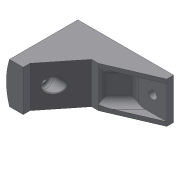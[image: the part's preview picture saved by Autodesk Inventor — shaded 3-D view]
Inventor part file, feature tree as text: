
AUTODESK INVENTOR PART (.ipt)
format: ipt  version: 2018 (Build 220112000, 112)  size: 190,464 bytes
history: native  units: mm
features: sketch x7, extrude x5, projected_geometry x5, fillet x3, hole x2, chamfer x2, mirror x1
ambient origin geometry x8: Origin, YZ Plane, XZ Plane, XY Plane, X Axis, Y Axis, Z Axis, Center Point
bodies: Solid1 (feature_tree)
feature tree (25):
  extrude  "Extrusion1"  Depth=30.0mm
  extrude  "Extrusion2"  Depth=70.0mm
  extrude  "Extrusion3"  Depth=30.0mm TaperAngle=0.0deg
  hole  "Hole1"  [1 undecoded]
  extrude  "Extrusion4"  Depth=3.0mm TaperAngle=0.0deg
  mirror  "Mirror1"
  chamfer  "Chamfer1"  Distance=2.0mm Angle=45.0deg
  fillet  "Fillet1"  Radius=5.0mm
  chamfer  "Chamfer2"  Distance=25.0mm Angle=45.0deg
  extrude  "Extrusion5"  Depth=10.0mm
  fillet  "Fillet2"  Radius=60.0mm
  fillet  "Fillet3"  Radius=0.5mm
  hole  "Hole2"  [1 undecoded]
  sketch  "Sketch1"  dims[d0=100.0mm d1=30.0mm]
  sketch  "Sketch2"  dims[d2=50.0mm d3=0.0mm d4=70.0mm]
  projected_geometry  "Projected Loop1"
  sketch  "Sketch3"  dims[d5=60.0mm d6=30.0mm d7=0.0mm]
  projected_geometry  "Projected Loop2"
  sketch  "Sketch4"  dims[d8=35.0mm d9=15.0mm d10=0.0mm]
  sketch  "Sketch5"  dims[d11=12.0mm]
  projected_geometry  "Projected Loop3"
  sketch  "Sketch6"  dims[d12=6.0mm d13=6.0mm d14=3.023mm d15=2.0mm d16=14.3117mm d17=8.0mm d18=20.594885mm d19=3.0mm d20=0.0mm d21=12.0mm d22=2.0mm d23=45.0deg d24=5.0mm d25=25.0mm d26=20.0mm d27=45.0deg]
  projected_geometry  "Projected Loop4"
  sketch  "Sketch7"  dims[d28=15.0mm d29=10.0mm d30=60.0mm d31=0.0mm d32=0.5mm d33=2.0mm d34=4.3mm d35=9.0mm d36=9.4mm d37=2.0mm d38=90.0deg d39=8.0mm d40=20.594885mm]
  projected_geometry  "Projected Loop5"
note: 2 required parameter values undecoded (feature->parameter linkage not recoverable at this tier; creation-order binding heuristic only, values carry confidence <= 0.55)
